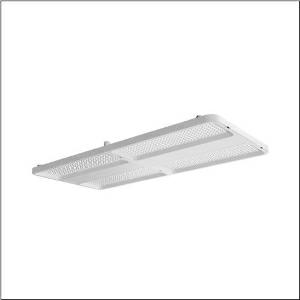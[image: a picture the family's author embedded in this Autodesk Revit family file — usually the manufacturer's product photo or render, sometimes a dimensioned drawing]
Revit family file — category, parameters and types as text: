
# Revit family: highbay_11_maxi_51hn12db5vda
name_source: partatom
category: Lighting Fixtures
units: mm (PartAtom-declared; Revit-internal decimal feet)

## family parameters
Cut with Voids When Loaded = No
Host = Face
Light Source = No
Part Type = Normal
Room Calculation Point = No
Round Connector Dimension = Use Diameter
Shared = No

## types (1)
- --- (1 x LED, 9030 lm, 44.6 W, 5000K)
    Apparent Load = 45 VA
    CIE Flux Codes = 87 98 100 100 100
    Color Rendering = 80
    Color Temperature = 5000K
    Default Elevation = 1800 mm
    Description = high bay luminaire Highbay 11 maxi; direct symmetric wide distribution, light control with lens of PMMA; UGR ≤ 22 (X = 4H | Y = 8H | S = 0.25H | reflection values 70/50/20); luminous flux: 55.810lm; light colour: 850, colour temperature: 5000K, MacAdam ≤ 2 SDCM (initial), colour rendering: CRI > 80; luminous efficacy: 189,3lm/W; rated service life: 100.000h (L95/B50) at AT= 25°C; control: DALI 2; luminaire connection: terminal, 5-pole, max. 2.5mm² (cable entry for one cable, Ø 8.5..16mm); mains connection: 230..240V, AC/DC 0/50..60Hz; connected load: 294,9W; protection rating (complete): IP66; insulation class (complete): insulation class I (protective earthing); protection symbol: D; impact resistance: IK08; certification: CE, ENEC, VDE, UKCA; luminaire for central battery installations according to DIN EN 60598-2-22, internal wiring halogen-free; luminaire LABS conformity tested according to VDMA 24364:2018-05; corresponds to IFS (International Featured Standards) requirements for safety and quality in the food industry; housing frame of high-performance plastic PA6, matt traffic white (RAL 9016); cover of PMMA; dimension (LxWxH): 946 x 442 x 72mm; permissible operating ambient temperature: -40..+50°C (reducing of maximum allowable ambient temperature of 5°C with ceiling mounting); packaging unit: 1 piece; (delivery without accessories; please order mounting accessories separately)
    Height = 72 mm  [stored 0.23622 ft]
    Lamp = 1 x LED
    Lamp Light Flux = 9030 lm
    Lamp Power = 44.6 W
    Lamp count = 1
    Length = 946 mm
    Luminous efficacy = 202 lm/W
    Manufacturer = Siteco
    ModVariant = No
    Model = 51HN12DB5VDA
    Mounting Place = Ceiling
    Mounting Type = Pendant
    Number of Poles = 1
    OnlyDefault = Yes
    Power Factor = 1
    Product Name = Highbay 11 maxi
    Product group = high bay luminaire
    ProductGroupID = 901
    Protection Class = Protection class I
    Protection Degree = IP 66
    RLX_Detail_Level = 1
    RLX_Emergency_Light_Flux = 0 lm
    RLX_Emergency_Type = 0
    RLX_Emergency_Type_DB = No
    RlxData = <blob elided: 127149 chars, md5=e262ef33>
    Socket = socket
    Standby Power = 0 W
    System Light Flux = 9030 lm
    System Power = 45 W
    Type Comments = : DC mode (central or group accumulator) initial emergency light level
    Type Image = l_1363244.jpg
    URL = http://relux.com
    VarID = @adj_006487
    Voltage = 0 V
    Weight = 0.00 kg
    Width = 442 mm

note: [stored X ft] marks values corroborated as IEEE doubles in the binary element streams (Revit-internal decimal feet)

## geometry (parser evidence)
native form markers: Blend x4, Sweep x9
no freeform markers — native parametric forms only
